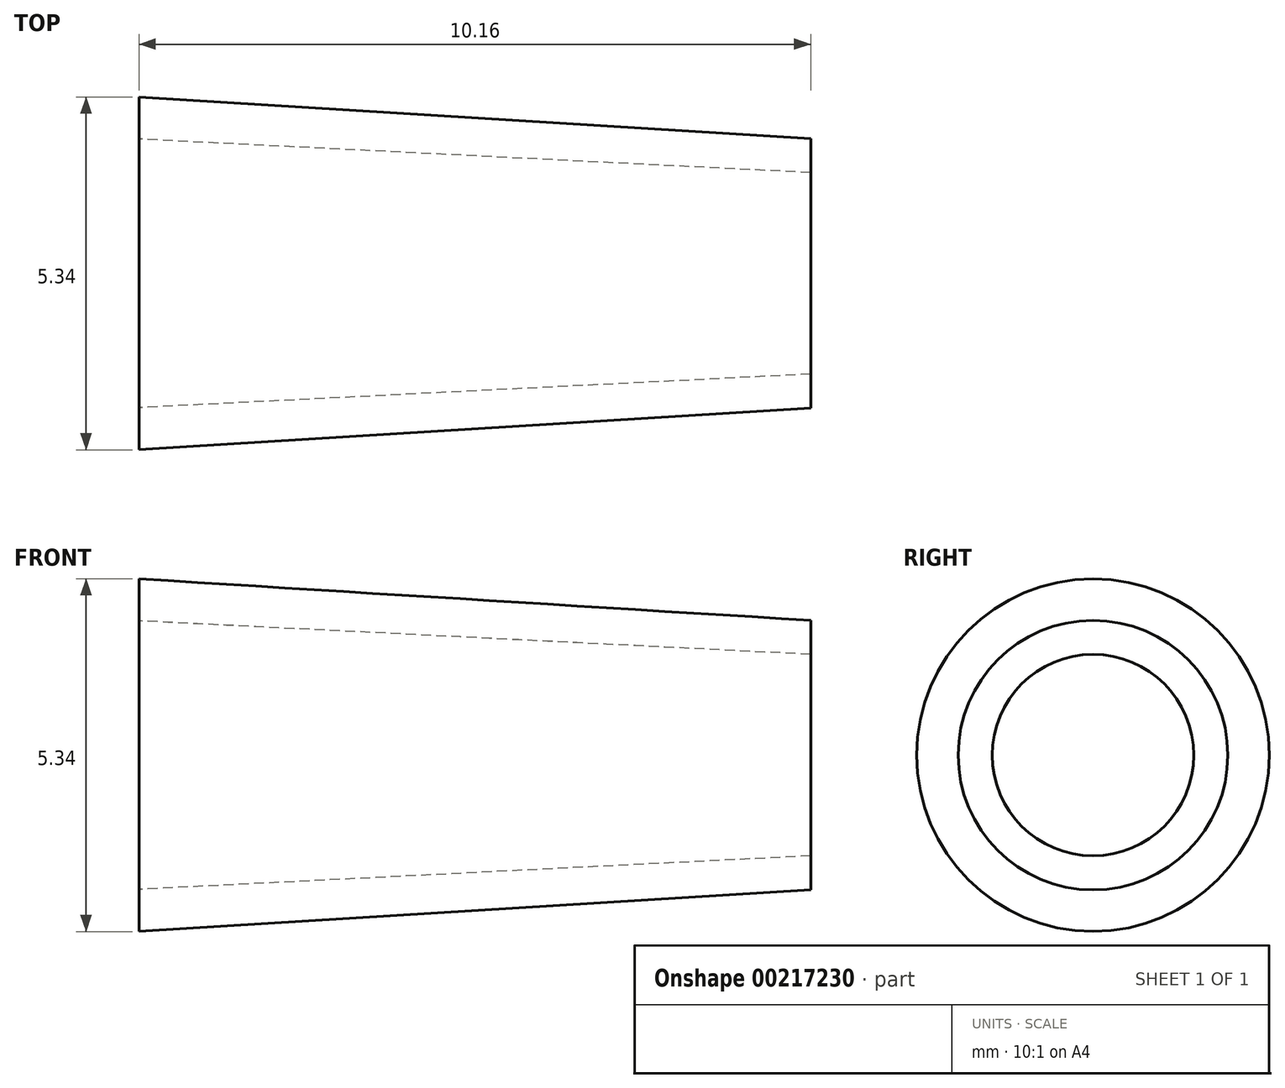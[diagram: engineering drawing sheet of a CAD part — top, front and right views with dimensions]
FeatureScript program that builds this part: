
annotation { "Feature Type Name" : "Feature", "Feature Type Description" : "" }
export const myFeature = defineFeature(function(context is Context, id is Id, definition is map)
    precondition{}
    {
        {
            var Q0;
            Q0=qCreatedBy(makeId("Top.planeOp"),FACE);
            var sketch = newSketch(context, id + "F0", { "sketchPlane" : qUnion([Q0])});
            skLineSegment(sketch, "E0", {"start": v(0, -2.03) * mm, "end": v(0, -2.67) * mm});
            skLineSegment(sketch, "E1", {"start": v(10.16, -1.52) * mm, "end": v(10.16, -2.04) * mm});
            skLineSegment(sketch, "E2", {"start": v(10.16, -2.04) * mm, "end": v(0, -2.67) * mm});
            skLineSegment(sketch, "E3", {"start": v(0, -2.03) * mm, "end": v(10.16, -1.52) * mm});
            skLineSegment(sketch, "E4", {"start": v(0, 0) * mm, "end": v(11.72, 0) * mm});
            skSolve(sketch);
        }
        {
            var Q0;
            Q0=makeQuery(id+"F0.imprint","IMPRINT",FACE,{"disambiguationData":[TD([[makeQuery(id+"F0.imprint","IMPRINT",EDGE,{"derivedFrom":sQuery(id+"F0.wireOp",EDGE,"E0")}),1.0]])]});
            var Q1;
            Q1=sQuery(id+"F0.wireOp",EDGE,"E4");
            revolve(context, id + "F1", {"entities" : qUnion([Q0]), "axis" : qUnion([Q1]), "revolveType" : RevolveType.FULL});
        }
    });
